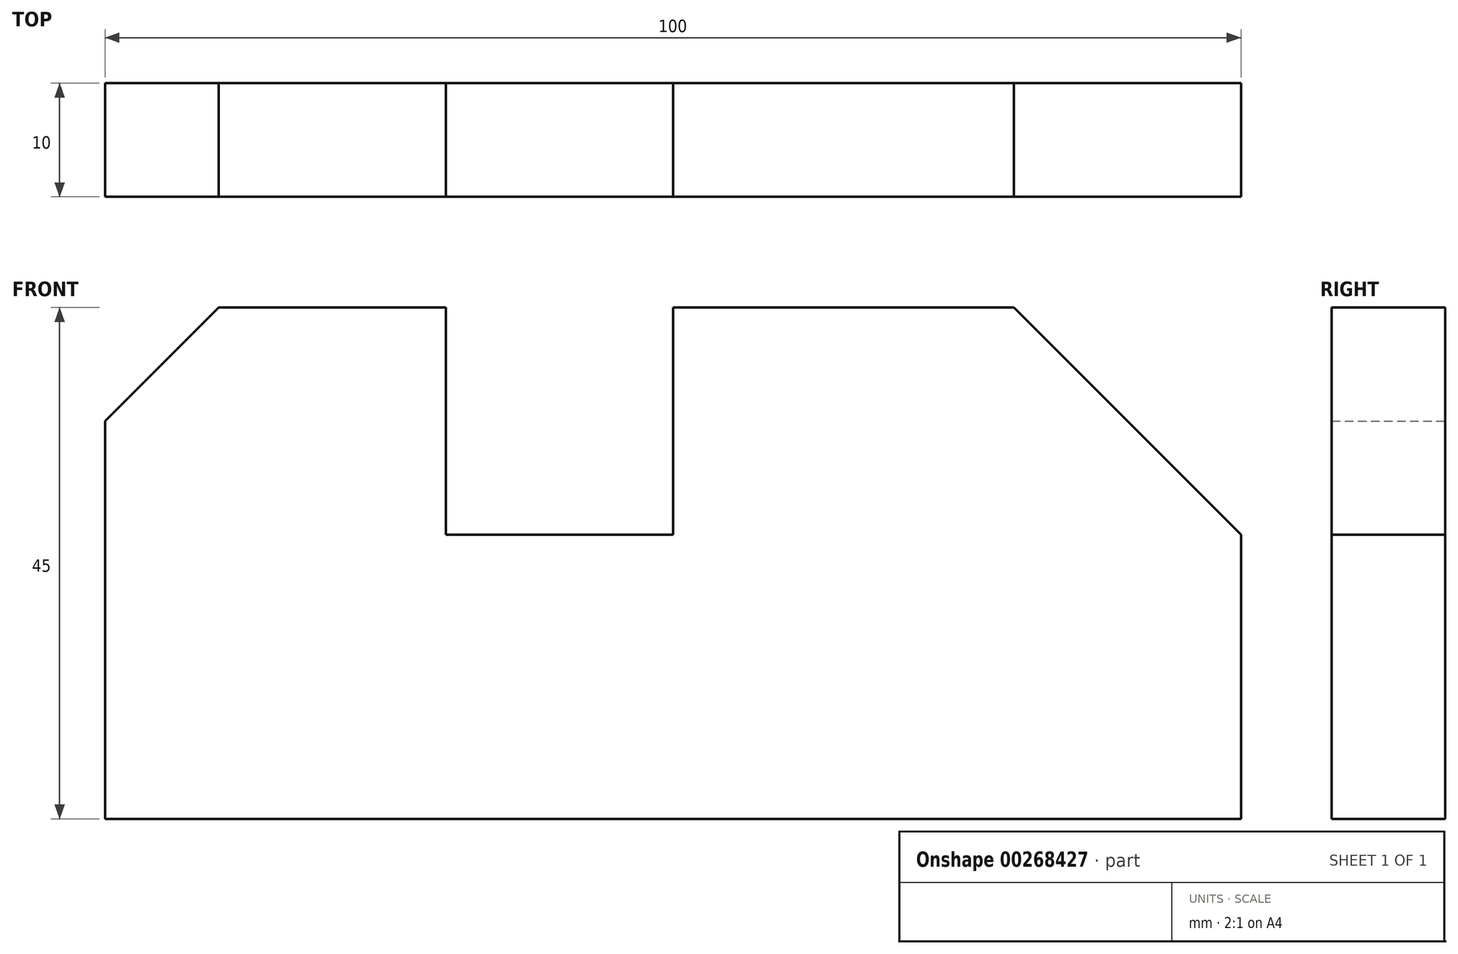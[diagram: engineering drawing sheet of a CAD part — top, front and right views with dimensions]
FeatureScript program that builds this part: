
annotation { "Feature Type Name" : "Feature", "Feature Type Description" : "" }
export const myFeature = defineFeature(function(context is Context, id is Id, definition is map)
    precondition{}
    {
        {
            var Q0;
            Q0=qCreatedBy(makeId("Front.planeOp"),FACE);
            var sketch = newSketch(context, id + "F0", { "sketchPlane" : qUnion([Q0])});
            skLineSegment(sketch, "E0", {"start": v(0, 0) * mm, "end": v(100, 0) * mm});
            skLineSegment(sketch, "E1", {"start": v(0, 0) * mm, "end": v(0, 35) * mm});
            skLineSegment(sketch, "E2", {"start": v(0, 35) * mm, "end": v(10, 45) * mm});
            skLineSegment(sketch, "E3", {"start": v(10, 45) * mm, "end": v(30, 45) * mm});
            skLineSegment(sketch, "E4", {"start": v(30, 45) * mm, "end": v(30, 25) * mm});
            skLineSegment(sketch, "E5", {"start": v(30, 25) * mm, "end": v(50, 25) * mm});
            skLineSegment(sketch, "E6", {"start": v(50, 25) * mm, "end": v(50, 45) * mm});
            skLineSegment(sketch, "E7", {"start": v(50, 45) * mm, "end": v(80, 45) * mm});
            skLineSegment(sketch, "E8", {"start": v(80, 45) * mm, "end": v(100, 25) * mm});
            skLineSegment(sketch, "E9", {"start": v(100, 25) * mm, "end": v(100, 0) * mm});
            skSolve(sketch);
        }
        {
            var Q0;
            Q0 = qSketchRegion(id + "F0", true);
            extrude(context, id + "F1", {"entities" : qUnion([Q0]), "depth" : 10 * mm});
        }
    });
